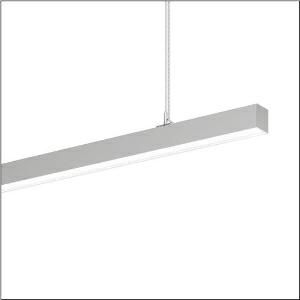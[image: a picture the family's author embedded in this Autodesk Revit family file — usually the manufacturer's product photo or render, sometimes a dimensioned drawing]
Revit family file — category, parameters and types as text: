
# Revit family: silica_r__21_51mx30db45sb_ca73
name_source: partatom
category: Lighting Fixtures
units: mm (PartAtom-declared; Revit-internal decimal feet)

## family parameters
Cut with Voids When Loaded = No
Host = Face
Light Source = No
Part Type = Normal
Room Calculation Point = No
Round Connector Dimension = Use Diameter
Shared = No

## types (1)
- --- (1 x LED, 5260 lm, 32 W, 4000K)
    Apparent Load = 32 VA
    CIE Flux Codes = 47 79 96 57 100
    Color Rendering = 80
    Color Temperature = 4000K
    Default Elevation = 1800 mm
    Description = Silica® 21, office luminaire, primary optical cover: cover, of PMMA, opal, light emission: direct/indirect distribution, primary light characteristic: symmetric, installation type: suspended mounting, LED, rated luminous flux: 5.260lm, luminous efficacy: 164lm/W, light colour: 840, colour temperature: 4000K, with terminal, 3+2-pole, max. 2.5mm², mains connection: 220..240V, AC, 50/60Hz, rated input power: 32W, luminaire housing, of aluminium, metallic grey (RAL 9006), length: 1.504mm, width: 53mm, height: 53mm, protection rating (complete): IP20, insulation class (complete): insulation class I (protective earthing), certification: CE, permissible operating ambient temperature: 0..+35°C, standard: EN 50419, packaging unit: 1 piece
    Height = 53 mm
    Lamp = 1 x LED
    Lamp Light Flux = 5260 lm
    Lamp Power = 32 W
    Lamp count = 1
    Length = 1504 mm
    Luminous efficacy = 164 lm/W
    Manufacturer = Siteco
    ModVariant = No
    Model = 51MX30DB45SB
    Mounting Place = Ceiling
    Mounting Type = Pendant
    Number of Poles = 1
    OnlyDefault = Yes
    Power Factor = 1
    Product Name = Silica® 21
    Product group = office luminaire | ceiling pendant
    ProductGroupID = 902
    Protection Class = Protection class I
    Protection Degree = IP 20
    RLX_Detail_Level = 1
    RLX_Emergency_Light_Flux = 0 lm
    RLX_Emergency_Type = 0
    RLX_Emergency_Type_DB = No
    RlxData = <blob elided: 23365 chars, md5=da436429>
    Socket = socket
    Standby Power = 0 W
    System Light Flux = 5260 lm
    System Power = 32 W
    Type Comments = factory setting: luminous flux: 100 % | dim-lin: 254 | 218 mA
    Type Image = l_1335864.jpg
    URL = http://relux.com
    VarID = @adj_085783
    Voltage = 0 V
    Weight = 0.00 kg
    Width = 53 mm

## geometry (parser evidence)
native form markers: Blend x4, Sweep x13
no freeform markers — native parametric forms only
